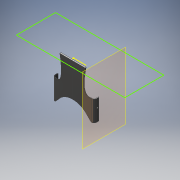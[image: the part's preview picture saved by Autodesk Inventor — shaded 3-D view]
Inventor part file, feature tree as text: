
AUTODESK INVENTOR PART (.ipt)
format: ipt  version: 2019 (Build 230136000, 136)  size: 1,406,464 bytes
history: native  units: mm
features: plane x28, sketch x26, extrude x12, mirror x7, fillet x7, loft x4, chamfer x3, projected_geometry x2, other x1
ambient origin geometry x8: Origin, YZ Plane, XZ Plane, XY Plane, X Axis, Y Axis, Z Axis, Center Point
bodies: Body1 (feature_tree)
feature tree (90):
  sketch  "Sketch1"  dims[d2=55.0mm d5=-107.0mm d13=5.0mm d14=50.0mm]
  plane  "Work Plane1"
  sketch  "Sketch2"  dims[d15=70.0mm d16=5.0mm]
  sketch  "Sketch3"  dims[d17=0.0mm d18=90.0deg d19=0.0mm d20=90.0deg d21=0.0mm d22=90.0deg d23=2.0mm]
  plane  "Work Plane2"
  loft  "Loft2"
  mirror  "Mirror2"
  fillet  "Fillet1"  Radius=5.0mm
  fillet  "Fillet4"  Radius=50.0mm
  plane  "Work Plane3"
  plane  "Work Plane4"
  extrude  "Extrusion1"  Depth=5.0mm
  plane  "Work Plane5"
  extrude  "Extrusion2"  TaperAngle=0.0deg  [1 undecoded]
  fillet  "Fillet5"  [1 undecoded]
  mirror  "Mirror3"
  plane  "Work Plane22"
  plane  "Work Plane6"
  plane  "Work Plane7"
  fillet  "Fillet11"  Radius=2.0mm
  extrude  "Extrusion7"  Depth=87.5mm
  mirror  "Mirror4"
  plane  "Work Plane8"
  plane  "Work Plane9"
  sketch  "Sketch20"  dims[d42=2.0mm]
  plane  "Work Plane10"
  sketch  "Sketch21"  dims[d43=2.0mm]
  plane  "Work Plane11"
  sketch  "Sketch22"  dims[d44=2.0mm]
  loft  "Loft5"
  plane  "Work Plane13"
  sketch  "Sketch25"  dims[d45=2.0mm]
  plane  "Work Plane18"
  loft  "Loft6"
  mirror  "Mirror5"
  plane  "Work Plane19"
  extrude  "Extrusion9"  Depth=2.0mm
  fillet  "Fillet12"  Radius=2.0mm
  fillet  "Fillet14"  Radius=2.0mm
  plane  "Work Plane20"
  plane  "Work Plane21"
  plane  "Work Plane23"
  plane  "Work Plane24"
  plane  "Work Plane25"
  sketch  "Sketch33"  dims[d48=2.0mm]
  plane  "Work Plane26"
  sketch  "Sketch34"  dims[d49=2.0mm d50=2.0mm d51=1.0mm]
  plane  "Work Plane27"
  sketch  "Sketch35"  dims[d79=-25.0mm]
  plane  "Work Plane30"
  sketch  "Sketch38"  dims[d84=2.0mm]
  plane  "Work Plane31"
  plane  "Work Plane35"
  chamfer  "Chamfer7"  Distance=2.0mm
  chamfer  "Chamfer8"  Distance=28.0mm
  chamfer  "Chamfer9"  Distance=22.0mm
  loft  "Loft10"
  mirror  "Mirror9"
  plane  "Work Plane37"
  sketch  "Sketch47"  dims[d85=13.5mm]
  extrude  "Extrusion25"  Depth=3.0mm
  extrude  "Extrusion26"  Depth=3.0mm
  extrude  "Extrusion27"  TaperAngle=0.0deg  [1 undecoded]
  plane  "Work Plane38"
  extrude  "Extrusion28"  TaperAngle=0.0deg  [1 undecoded]
  extrude  "Extrusion29"  [1 undecoded]
  extrude  "Extrusion30"  Depth=2.0mm
  plane  "Work Plane39"
  extrude  "Extrusion31"  Depth=10.0mm
  fillet  "Fillet19"  Radius=8.0mm
  mirror  "Mirror10"
  mirror  "Mirror11"
  extrude  "Extrusion32"  TaperAngle=0.0deg  [1 undecoded]
  sketch  "Sketch4"  dims[d29=1.0mm d30=-4.5mm d31=87.5mm]
  sketch  "Sketch5"  dims[d32=0.0mm d33=0.0mm d34=-28.0mm]
  sketch  "Sketch6"  dims[d35=15.0mm d36=3.0mm]
  sketch  "Sketch17"  dims[d37=0.0mm d38=0.0mm d39=2.0mm d40=2.0mm d41=2.0mm]
  sketch  "Sketch27"  dims[d46=2.0mm]
  other  "Edges1"
  sketch  "Sketch28"  dims[d47=2.0mm]
  sketch  "Sketch48"  dims[d86=2.5mm]
  sketch  "Sketch49"  dims[d87=5.0mm]
  sketch  "Sketch50"  dims[d88=6.25mm d89=28.0mm d90=0.0mm d91=22.0mm d101=200.0mm]
  sketch  "Sketch51"  dims[d104=5.0mm d105=50.0mm d106=-80.0mm d107=45.0mm]
  sketch  "Sketch52"  dims[d108=3.0mm d109=70.0mm]
  sketch  "Sketch53"  dims[d110=80.0mm d111=3.0mm]
  sketch  "Sketch54"  dims[d112=20.0mm d123=0.0mm d124=90.0deg]
  projected_geometry  "Projected Loop1"
  sketch  "Sketch55"  dims[d125=0.0mm d126=90.0deg d127=0.0mm d128=90.0deg d129=-20.0mm d131=2.0mm d132=80.0mm d133=8.0mm d134=0.0mm d135=0.0mm d136=90.0deg d137=0.0mm d138=90.0deg d139=0.0mm d140=90.0deg d141=3.0mm d142=7.0mm d143=10.0mm d144=0.0mm d145=70.0mm d147=10.0mm d171=35.75mm d174=-8.25mm d177=20.0mm d179=30.0mm d180=5.0mm d181=41.5mm d182=15.0mm d183=10.0mm d184=5.0mm d200=-2.0mm d219=15.0mm d241=2.0mm d242=2.0mm d243=45.0deg d244=1.0mm d245=2.0mm d246=45.0deg d247=0.5mm d248=2.0mm d249=45.0deg d250=5.0mm d251=0.0mm d252=90.0deg d253=0.0mm d254=90.0deg d255=0.0mm d256=90.0deg d263=10.0mm d264=0.0mm d265=5.0mm d266=0.0mm d267=4.0mm d268=20.0mm d269=0.0mm d270=16.0mm d271=14.0mm d272=20.0mm d273=0.0mm d274=4.0mm d275=20.0mm d276=0.0mm d277=0.0mm d278=0.0mm d279=75.5mm d280=10.0mm d281=0.0mm d282=3.0mm d283=4.0mm d284=10.0mm d285=0.0mm]
  projected_geometry  "Projected Loop2"
note: 6 required parameter values undecoded (feature->parameter linkage not recoverable at this tier; creation-order binding heuristic only, values carry confidence <= 0.55)
